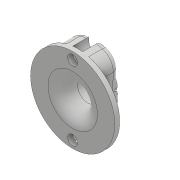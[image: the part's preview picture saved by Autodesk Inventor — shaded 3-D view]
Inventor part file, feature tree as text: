
AUTODESK INVENTOR PART (.ipt)
format: ipt  version: 2017 (Build 210142000, 142)  size: 256,512 bytes
history: native  units: mm
features: sketch x7, extrude x6, fillet x4, projected_geometry x2, hole x1, chamfer x1
ambient origin geometry x8: Origin, YZ Plane, XZ Plane, XY Plane, X Axis, Y Axis, Z Axis, Center Point
bodies: Solid1 (feature_tree)
feature tree (21):
  extrude  "Extrusion1"  Depth=2.0mm TaperAngle=0.0deg
  extrude  "Extrusion2"  Depth=6.0mm
  fillet  "Fillet1"  Radius=4.0mm
  extrude  "Extrusion3"  Depth=2.0mm
  extrude  "Extrusion4"  Depth=2.0mm TaperAngle=0.0deg
  hole  "Hole1"  [1 undecoded]
  fillet  "Fillet2"  Radius=14.0mm
  extrude  "Extrusion5"  Depth=6.0mm
  chamfer  "Chamfer1"  Distance=18.0mm
  extrude  "Extrusion6"  Depth=2.5mm TaperAngle=0.0deg
  fillet  "Fillet3"  Radius=8.0mm
  fillet  "Fillet4"  Radius=7.0mm
  sketch  "Sketch1"  dims[d0=34.0mm d1=2.0mm d2=0.0mm]
  sketch  "Sketch2"  dims[d3=8.0mm d4=6.0mm d5=4.0mm]
  sketch  "Sketch3"  dims[d6=4.0mm d7=0.0mm d8=2.0mm]
  sketch  "Sketch4"  dims[d9=8.0mm d10=2.0mm d11=0.0mm]
  projected_geometry  "Projected Loop1"
  sketch  "Sketch5"  dims[d12=8.0mm d13=0.0mm d14=14.0mm d15=14.0mm]
  sketch  "Sketch6"  dims[d16=4.0mm d17=6.0mm d18=4.0mm d19=2.0mm d20=90.0deg d21=8.0mm d22=20.594885mm d23=6.0mm]
  sketch  "Sketch7"  dims[d24=18.0mm d25=18.0mm d26=8.0mm d27=0.0mm d28=8.0mm d29=2.0mm d30=45.0deg d31=7.0mm d32=7.0mm d33=8.0mm d34=0.0mm d35=6.0mm d36=2.5mm]
  projected_geometry  "Projected Loop2"
note: 1 required parameter value undecoded (feature->parameter linkage not recoverable at this tier; creation-order binding heuristic only, values carry confidence <= 0.55)
